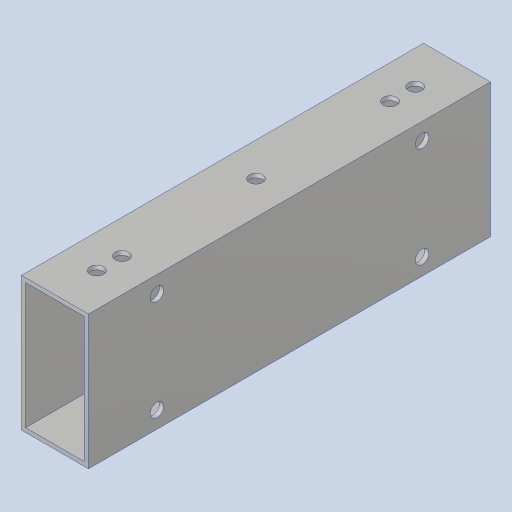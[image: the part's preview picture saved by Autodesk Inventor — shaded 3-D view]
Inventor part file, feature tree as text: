
AUTODESK INVENTOR PART (.ipt)
format: ipt  version: 2023.4 (Build 274418000, 418)  size: 264,704 bytes
history: native  units: in
note: dims shown in document units (in); Inventor stores cm internally (conversion verified against a paired STEP export)
features: hole x4, sketch x4, extrude x1, projected_geometry x1
ambient origin geometry x8: Origin, YZ Plane, XZ Plane, XY Plane, X Axis, Y Axis, Z Axis, Center Point
bodies: Solid1 (feature_tree)
feature tree (10):
  extrude  "Extrusion1"  Depth=4.0in
  hole  "Hole1"  [1 undecoded]
  hole  "Hole3"  [1 undecoded]
  hole  "Hole4"  [1 undecoded]
  hole  "Hole2"  [1 undecoded]
  sketch  "Sketch2"  dims[d4=0.0in d5=4.0in]
  projected_geometry  "Projected Loop1"
  sketch  "Sketch3"  dims[d6=0.201in d7=0.75in d8=0.385in d9=0.25in d10=0.5635in d11=1.0in d12=0.8108in d14=4.7244in]
  sketch  "Sketch4"  dims[d15=3.7402in d16=4.2323in]
  sketch  "Sketch5"  dims[d17=1.5in d18=0.156in d19=0.38in d20=0.375in d21=0.25in d22=0.5635in d23=1.0in d24=0.8108in d25=4.2323in d28=1.5in d29=0.201in d30=0.38in d31=0.385in d32=0.25in d33=0.5635in d34=1.0in d35=0.8108in d36=4.75in d37=0.201in d38=0.75in d39=0.385in d40=0.25in d41=0.5635in d42=1.0in d43=0.8108in]
note: 4 required parameter values undecoded (feature->parameter linkage not recoverable at this tier; creation-order binding heuristic only, values carry confidence <= 0.55)
